SOLIDWORKS PART (.sldprt)
format: sldprt  version: not decoded by parser v0  size: 90,112 bytes
history: native  units: mm
features: plane x4, sketch x3, extrude x2, material x1, dome x1, cut_extrude x1 (+13 scaffold rows collapsed)
feature tree (25):
  scaffold x13  (default folders/planes/origin — collapsed)
  material  "材质 <未指定>"
  plane  "前视基准面"
  plane  "上视基准面"
  plane  "右视基准面"
  sketch  "草图1"
  extrude  "凸台-拉伸1"  Depth=1.5mm
  sketch  "草图2"  dims[D2=1.0mm D1=0.0mm]
  extrude  "凸台-拉伸2"  Depth=0.05mm
  dome  "圆顶1"
  plane  "基准面1"  Offset=0.1mm
  sketch  "草图3"  dims[D1=0.05mm D2=0.05mm]
  cut_extrude  "切除-拉伸1"  Depth=3.12mm
decode coverage: 5 of 7 modeling features carry decoded parameters
note: suppression state not decoded; provenance and decode notes live in map.json
